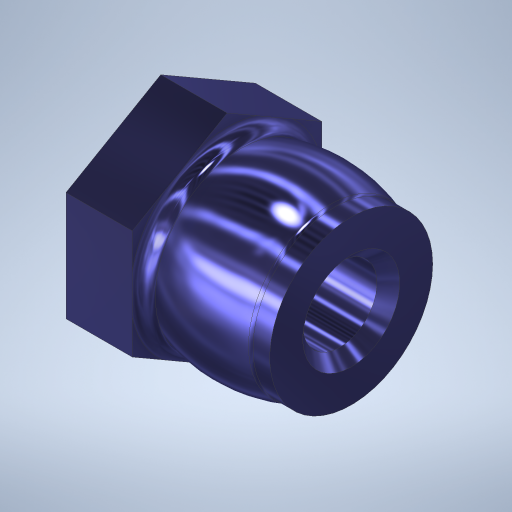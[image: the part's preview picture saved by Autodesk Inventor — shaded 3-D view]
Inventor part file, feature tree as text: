
AUTODESK INVENTOR PART (.ipt)
format: ipt  version: 2023.1 (Build 271208000, 208)  size: 386,048 bytes
history: native  units: in
note: dims shown in document units (in); Inventor stores cm internally (conversion verified against a paired STEP export)
features: sketch x3, extrude x2, revolve x1, fillet x1, chamfer x1
ambient origin geometry x8: Origin, YZ Plane, XZ Plane, XY Plane, X Axis, Y Axis, Z Axis, Center Point
bodies: Solid1 (feature_tree)
feature tree (8):
  revolve  "Revolution1"  [1 undecoded]
  extrude  "Extrusion1"  Depth=0.0875in
  extrude  "Extrusion2"  Depth=0.015in
  fillet  "Fillet1"  [1 undecoded]
  chamfer  "Chamfer1"  Distance=1.0in
  sketch  "Sketch1"  dims[d0=0.25in d1=0.2in]
  sketch  "Sketch2"  dims[d2=0.157in d3=0.0875in]
  sketch  "Sketch3"  dims[d5=0.098in d6=0.2151in d7=90.0deg d8=1.0in d9=0.0in d10=0.025in d11=0.0in d12=0.015in d13=0.015in d14=0.125in d15=45.0deg]
note: 2 required parameter values undecoded (feature->parameter linkage not recoverable at this tier; creation-order binding heuristic only, values carry confidence <= 0.55)